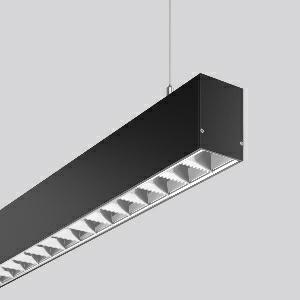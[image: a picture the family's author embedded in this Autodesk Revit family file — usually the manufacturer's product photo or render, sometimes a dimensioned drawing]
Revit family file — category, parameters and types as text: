
# Revit family: less_is_more_50_312335_003_1_8df0
name_source: partatom
category: Lighting Fixtures
units: mm (PartAtom-declared; Revit-internal decimal feet)

## family parameters
Cut with Voids When Loaded = No
Host = Face
Light Source = No
Part Type = Normal
Room Calculation Point = No
Round Connector Dimension = Use Diameter
Shared = No

## types (1)
- LESS IS MORE 50 (1 x LED Modul 840, 2650 lm, 4000)
    Apparent Load = 22 VA
    CIE Flux Codes = 95 100 100 100 100
    Color Rendering = 80
    Color Temperature = 4000
    Default Elevation = 1800 mm
    Description = Series: LESS IS MORE 50
Linear pendant luminaire for aesthetically sophisticated lighting. Housing: extruded aluminium profile, powder-coated. End cap aluminium powder-coated. Canopy made of aluminium, powder-coated. Alea optical system: Reflector structure (ABS, Aluminium-coated, highly polished) with integrated diffuser made of non-yellowing plastic (PMMA) opal for glare-free light at the workstation (screen-compliant according to EN 12464-1). Direct light emission. Suitable for pendant. 2-point steel cable suspension freely positionable and infinitely height-adjustable. Special lengths available on request. LED unit with integrated converter interchangeable and removable. Suitable for through-wiring. With sensors or as a safety luminaire on request. 
Colour: deep black, matt (RAL 9005)
Length: 847 mm
Width: 57 mm
Height: 75 mm
Suspension length: 2000 mm
Lamp: LED
Socket: without socket
Colour temperature: 4000K
Colour rendering index (CRI): 80
System power: 22 W
Rated luminous flux: 2650 lm
Luminous efficiency: 120 lm/W
Control gear: Regulated power supply
Protection class: I
Type of protection: IP 20
    Height = 75 mm
    Lamp = 1 x LED Modul 840
    Lamp Light Flux = 2650 lm
    Lamp count = 1
    Length = 847 mm
    Lifetime = 50000 h
    Luminous efficacy = 120 lm/W
    Manufacturer = RZB
    ModVariant = No
    Model = 312335.003.1
    Mounting Place = Ceiling
    Mounting Type = Pendant
    Number of Poles = 1
    OnlyDefault = Yes
    Power Factor = 1
    Product Name = LESS IS MORE 50
    Product group = Pendant LED linear luminaires
    ProductGroupID = 907
    Protection Class = Protection class I
    Protection Degree = IP 20
    RLX_Detail_Level = 1
    RLX_Emergency_Light_Flux = 0 lm
    RLX_Emergency_Type = 0
    RLX_Emergency_Type_DB = No
    RlxData = <blob elided: 39529 chars, md5=28ae3874>
    Socket = socket
    Standby Power = 0 W
    System Light Flux = 2650 lm
    System Power = 22 W
    Type Comments = Product without accessories
    Type Image = 312342.003.jpg
    URL = http://relux.com
    VarID = ---
    Voltage = 230 V
    Voltage Range = 220-240 V
    Weight = 0.00 kg
    Width = 57 mm

## geometry (parser evidence)
native form markers: Blend x4, Sweep x9
no freeform markers — native parametric forms only
